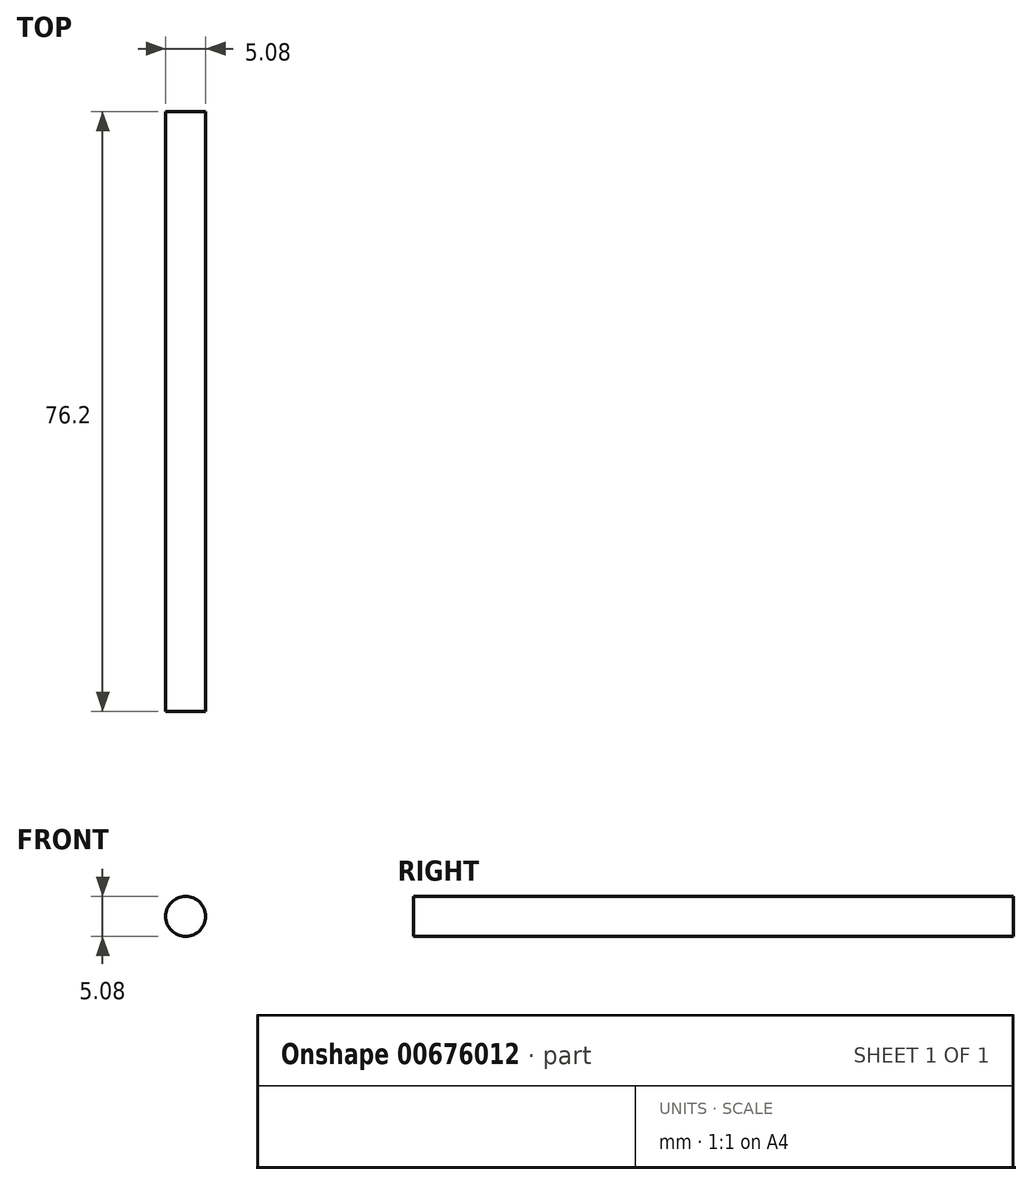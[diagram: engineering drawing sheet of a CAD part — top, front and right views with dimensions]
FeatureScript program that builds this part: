
annotation { "Feature Type Name" : "Feature", "Feature Type Description" : "" }
export const myFeature = defineFeature(function(context is Context, id is Id, definition is map)
    precondition{}
    {
        {
            var Q0;
            Q0=qCreatedBy(makeId("Front.planeOp"),FACE);
            var sketch = newSketch(context, id + "F0", { "sketchPlane" : qUnion([Q0])});
            skCircle(sketch, "E0", {"center": v(0, 0) * mm, "radius": 2.54 * mm});
            skSolve(sketch);
        }
        {
            var Q0;
            Q0 = qSketchRegion(id + "F0", true);
            extrude(context, id + "F1", {"entities" : qUnion([Q0]), "depth" : 76.2 * mm, "offsetDistance" : 25.4 * mm});
        }
    });
